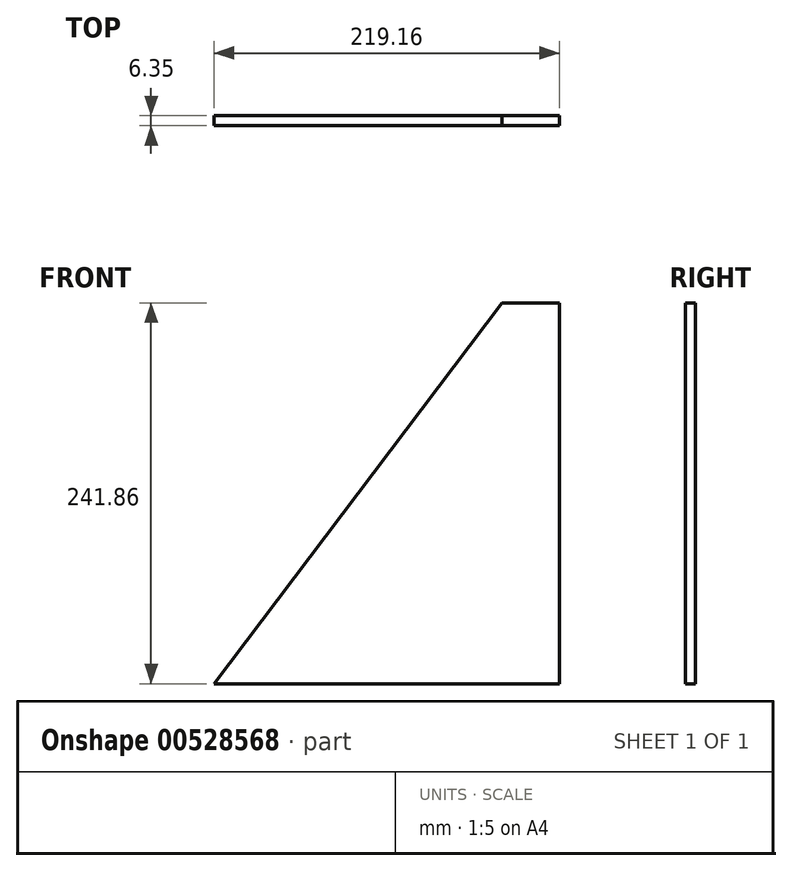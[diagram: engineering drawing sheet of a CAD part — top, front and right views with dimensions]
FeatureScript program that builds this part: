
annotation { "Feature Type Name" : "Feature", "Feature Type Description" : "" }
export const myFeature = defineFeature(function(context is Context, id is Id, definition is map)
    precondition{}
    {
        {
            var Q0;
            Q0=qCreatedBy(makeId("Front.planeOp"),FACE);
            var sketch = newSketch(context, id + "F0", { "sketchPlane" : qUnion([Q0])});
            skLineSegment(sketch, "E0", {"start": v(0, 0) * mm, "end": v(219.16, 0) * mm});
            skLineSegment(sketch, "E1", {"start": v(219.16, 0) * mm, "end": v(219.16, 241.86) * mm});
            skLineSegment(sketch, "E2", {"start": v(219.16, 241.86) * mm, "end": v(182.65, 241.86) * mm});
            skLineSegment(sketch, "E3", {"start": v(182.65, 241.86) * mm, "end": v(0, 0) * mm});
            skSolve(sketch);
        }
        {
            var Q0;
            Q0 = qSketchRegion(id + "F0", true);
            extrude(context, id + "F1", {"entities" : qUnion([Q0]), "depth" : 6.35 * mm, "offsetDistance" : 25.4 * mm});
        }
    });
